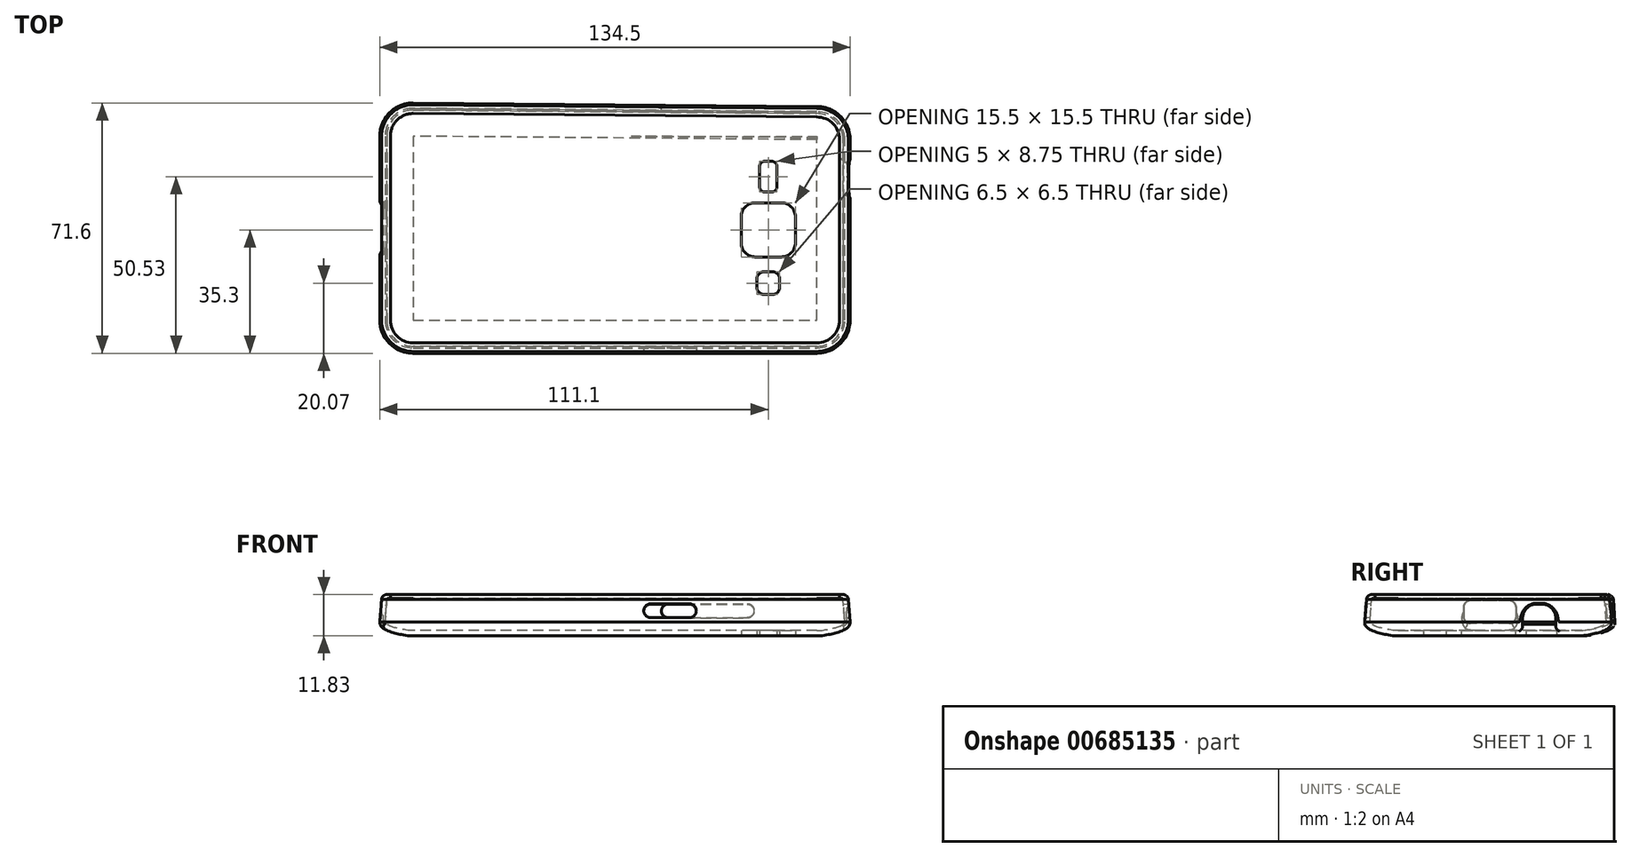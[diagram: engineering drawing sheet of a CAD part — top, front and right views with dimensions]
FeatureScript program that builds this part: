
annotation { "Feature Type Name" : "Feature", "Feature Type Description" : "" }
export const myFeature = defineFeature(function(context is Context, id is Id, definition is map)
    precondition{}
    {
        {
            var Q0;
            Q0=qCreatedBy(makeId("Front.planeOp"),FACE);
            var sketch = newSketch(context, id + "F0", { "sketchPlane" : qUnion([Q0])});
            skFitSpline(sketch, "E0", {"points": [v(23.24, 0) * mm, v(26.98, 0.47) * mm, v(29.38, 1.12) * mm, v(31.08, 2) * mm, v(31.24, 2.46) * mm], "startDerivative": vector(11.56, 0) * mm, "endDerivative": vector(0, 3.86) * mm});
            skFitSpline(sketch, "E1", {"points": [v(30.74, 9) * mm, v(30.63, 9.1) * mm, v(30.38, 9.18) * mm, v(29.74, 9.2) * mm], "startDerivative": vector(0.08, 0.24) * mm, "endDerivative": vector(-0.18, 0) * mm});
            skFitSpline(sketch, "E2.0", {"points": [v(32.24, 8.88) * mm, v(32.24, 8.97) * mm, v(32.22, 9.13) * mm, v(32.16, 9.35) * mm, v(32.08, 9.51) * mm, v(32, 9.63) * mm, v(31.92, 9.73) * mm, v(31.85, 9.8) * mm, v(31.78, 9.87) * mm, v(31.73, 9.91) * mm, v(31.67, 9.96) * mm, v(31.62, 10) * mm, v(31.56, 10.04) * mm, v(31.44, 10.12) * mm, v(31.23, 10.21) * mm, v(31.02, 10.27) * mm, v(30.85, 10.3) * mm, v(30.7, 10.31) * mm, v(30.58, 10.32) * mm, v(30.46, 10.32) * mm, v(30.34, 10.33) * mm, v(30.23, 10.33) * mm, v(30.15, 10.33) * mm, v(30.1, 10.33) * mm, v(30.06, 10.33) * mm, v(30.04, 10.33) * mm, v(30.04, 10.33) * mm, v(30.03, 10.33) * mm]});
            skFitSpline(sketch, "E3.0", {"points": [v(23.24, -1.5) * mm, v(23.79, -1.5) * mm, v(24.58, -1.45) * mm, v(25.58, -1.32) * mm, v(26.3, -1.2) * mm, v(26.96, -1.07) * mm, v(27.57, -0.94) * mm, v(28.15, -0.8) * mm, v(28.72, -0.66) * mm, v(29.28, -0.5) * mm, v(29.86, -0.3) * mm, v(30.45, -0.08) * mm, v(30.94, 0.14) * mm, v(31.32, 0.33) * mm, v(31.6, 0.5) * mm, v(31.84, 0.67) * mm, v(32.03, 0.83) * mm, v(32.19, 0.98) * mm, v(32.34, 1.16) * mm, v(32.51, 1.43) * mm, v(32.67, 1.8) * mm, v(32.74, 2.2) * mm, v(32.74, 2.39) * mm, v(32.74, 2.46) * mm]});
            skLineSegment(sketch, "E4", {"start": v(30.07, 10.33) * mm, "end": v(29.74, 10.33) * mm});
            skLineSegment(sketch, "E5", {"start": v(29.74, 10.33) * mm, "end": v(29.74, 9.2) * mm});
            skLineSegment(sketch, "E6", {"start": v(23.24, 0) * mm, "end": v(23.24, -1.5) * mm});
            skLineSegment(sketch, "E7", {"start": v(32.24, 8.88) * mm, "end": v(32.74, 2.46) * mm});
            skLineSegment(sketch, "E8", {"start": v(31.24, 2.46) * mm, "end": v(30.74, 9) * mm});
            skSolve(sketch);
        }
        {
            var Q0;
            Q0=makeQuery(id+"F0.imprint","IMPRINT",FACE,{"disambiguationData":[TD([[makeQuery(id+"F0.imprint","IMPRINT",EDGE,{"derivedFrom":sQuery(id+"F0.wireOp",EDGE,"E0")}),-1.0]])]});
            extrude(context, id + "F1", {"entities" : qUnion([Q0]), "depth" : 51.6 * mm, "offsetDistance" : 25 * mm});
        }
        {
            var Q0;
            Q0=makeQuery(id+"F1.opExtrude","CAP_FACE",FACE,{"disambiguationData":[OSD([sQuery(id+"F0.wireOp",EDGE,"E0"),sQuery(id+"F0.wireOp",EDGE,"iwZR0FTT-lc6u-Gi5J-cjGM-f3HXfoQX6Iv2"),sQuery(id+"F0.wireOp",EDGE,"E1"),sQuery(id+"F0.wireOp",EDGE,"E2.0"),sQuery(id+"F0.wireOp",EDGE,"E3.0"),sQuery(id+"F0.wireOp",EDGE,"E4"),sQuery(id+"F0.wireOp",EDGE,"E5"),sQuery(id+"F0.wireOp",EDGE,"E6"),sQuery(id+"F0.wireOp",EDGE,"pERrGrT5-6ted-8LdD-2vIX-14O5lISJ3Ztg")])],"isStart":false});
            var Q1;
            Q1=makeQuery(id+"F1.opExtrude","CAP_EDGE",EDGE,{"disambiguationData":[OSD([sQuery(id+"F0.wireOp",EDGE,"E6")])],"isStart":false});
            revolve(context, id + "F2", {"operationType" : NewBodyOperationType.ADD, "entities" : qUnion([Q0]), "axis" : qUnion([Q1]), "revolveType" : RevolveType.ONE_DIRECTION, "angle" : 90 * degree});
        }
        {
            var Q0;
            {var subQ0=sQuery(id+"F0.wireOp",EDGE,"E6");Q0=makeQuery(id+"F2.boolean.opBoolean","MERGE",FACE,{"derivedFrom":[makeQuery(id+"F1.opExtrude","SWEPT_FACE",FACE,{"disambiguationData":[OSD([subQ0])]}),makeQuery(id+"F2.opRevolve","CAP_FACE",FACE,{"disambiguationData":[OSD([sQuery(id+"F0.wireOp",EDGE,"E0"),sQuery(id+"F0.wireOp",EDGE,"iwZR0FTT-lc6u-Gi5J-cjGM-f3HXfoQX6Iv2"),sQuery(id+"F0.wireOp",EDGE,"E1"),sQuery(id+"F0.wireOp",EDGE,"E2.0"),sQuery(id+"F0.wireOp",EDGE,"E3.0"),sQuery(id+"F0.wireOp",EDGE,"E4"),sQuery(id+"F0.wireOp",EDGE,"E5"),subQ0,sQuery(id+"F0.wireOp",EDGE,"pERrGrT5-6ted-8LdD-2vIX-14O5lISJ3Ztg")])],"isStart":false})]});}
            var sketch = newSketch(context, id + "F3", { "sketchPlane" : qUnion([Q0])});
            skLineSegment(sketch, "E9", {"start": v(51.6, 0) * mm, "end": v(51.6, -1.5) * mm});
            skSolve(sketch);
        }
        {
            var Q0;
            Q0=makeQuery(id+"F3.imprint","IMPRINT",FACE,{"disambiguationData":[TD([[makeQuery(id+"F3.imprint","IMPRINT",EDGE,{"derivedFrom":sQuery(id+"F3.wireOp",EDGE,"E9")}),1.0]])]});
            extrude(context, id + "F4", {"entities" : qUnion([Q0]), "operationType" : NewBodyOperationType.ADD, "depth" : 115.5 * mm, "offsetDistance" : 25 * mm});
        }
        {
            var Q0;
            Q0=makeQuery(id+"F4.opExtrude","CAP_FACE",FACE,{"disambiguationData":[OSD([sQuery(id+"F0.wireOp",EDGE,"E0"),sQuery(id+"F0.wireOp",EDGE,"iwZR0FTT-lc6u-Gi5J-cjGM-f3HXfoQX6Iv2"),sQuery(id+"F0.wireOp",EDGE,"E1"),sQuery(id+"F0.wireOp",EDGE,"E2.0"),sQuery(id+"F0.wireOp",EDGE,"E3.0"),sQuery(id+"F0.wireOp",EDGE,"E4"),sQuery(id+"F0.wireOp",EDGE,"E5"),sQuery(id+"F0.wireOp",EDGE,"pERrGrT5-6ted-8LdD-2vIX-14O5lISJ3Ztg"),sQuery(id+"F3.wireOp",EDGE,"E9")])],"isStart":false});
            var Q1;
            Q1=makeQuery(id+"F4.opExtrude","CAP_EDGE",EDGE,{"disambiguationData":[OSD([sQuery(id+"F3.wireOp",EDGE,"E9")])],"isStart":false});
            revolve(context, id + "F5", {"operationType" : NewBodyOperationType.ADD, "entities" : qUnion([Q0]), "axis" : qUnion([Q1]), "revolveType" : RevolveType.ONE_DIRECTION, "angle" : 90 * degree});
        }
        {
            var Q0;
            {var subQ0=sQuery(id+"F3.wireOp",EDGE,"E9");Q0=makeQuery(id+"F5.boolean.opBoolean","MERGE",FACE,{"derivedFrom":[makeQuery(id+"F4.opExtrude","SWEPT_FACE",FACE,{"disambiguationData":[OSD([subQ0])]}),makeQuery(id+"F5.opRevolve","CAP_FACE",FACE,{"disambiguationData":[OSD([sQuery(id+"F0.wireOp",EDGE,"E0"),sQuery(id+"F0.wireOp",EDGE,"iwZR0FTT-lc6u-Gi5J-cjGM-f3HXfoQX6Iv2"),sQuery(id+"F0.wireOp",EDGE,"E1"),sQuery(id+"F0.wireOp",EDGE,"E2.0"),sQuery(id+"F0.wireOp",EDGE,"E3.0"),sQuery(id+"F0.wireOp",EDGE,"E4"),sQuery(id+"F0.wireOp",EDGE,"E5"),sQuery(id+"F0.wireOp",EDGE,"pERrGrT5-6ted-8LdD-2vIX-14O5lISJ3Ztg"),subQ0])],"isStart":false})]});}
            var sketch = newSketch(context, id + "F6", { "sketchPlane" : qUnion([Q0])});
            skLineSegment(sketch, "E10", {"start": v(92.26, 0) * mm, "end": v(92.26, -1.5) * mm});
            skSolve(sketch);
        }
        {
            var Q0;
            Q0=makeQuery(id+"F6.imprint","IMPRINT",FACE,{"disambiguationData":[TD([[makeQuery(id+"F6.imprint","IMPRINT",EDGE,{"derivedFrom":sQuery(id+"F6.wireOp",EDGE,"E10")}),1.0]])]});
            extrude(context, id + "F7", {"entities" : qUnion([Q0]), "operationType" : NewBodyOperationType.ADD, "depth" : 52.6 * mm, "offsetDistance" : 25 * mm});
        }
        {
            var Q0;
            Q0=makeQuery(id+"F7.opExtrude","CAP_FACE",FACE,{"disambiguationData":[OSD([sQuery(id+"F0.wireOp",EDGE,"E0"),sQuery(id+"F0.wireOp",EDGE,"iwZR0FTT-lc6u-Gi5J-cjGM-f3HXfoQX6Iv2"),sQuery(id+"F0.wireOp",EDGE,"E1"),sQuery(id+"F0.wireOp",EDGE,"E2.0"),sQuery(id+"F0.wireOp",EDGE,"E3.0"),sQuery(id+"F0.wireOp",EDGE,"E4"),sQuery(id+"F0.wireOp",EDGE,"E5"),sQuery(id+"F0.wireOp",EDGE,"pERrGrT5-6ted-8LdD-2vIX-14O5lISJ3Ztg"),sQuery(id+"F6.wireOp",EDGE,"E10")])],"isStart":false});
            var Q1;
            Q1=makeQuery(id+"F7.opExtrude","CAP_EDGE",EDGE,{"disambiguationData":[OSD([sQuery(id+"F6.wireOp",EDGE,"E10")])],"isStart":false});
            revolve(context, id + "F8", {"operationType" : NewBodyOperationType.ADD, "entities" : qUnion([Q0]), "axis" : qUnion([Q1]), "revolveType" : RevolveType.ONE_DIRECTION, "angle" : 90.5 * degree});
        }
        {
            var Q0;
            Q0=makeQuery(id+"F1.opExtrude","CAP_FACE",FACE,{"disambiguationData":[OSD([sQuery(id+"F0.wireOp",EDGE,"E0"),sQuery(id+"F0.wireOp",EDGE,"iwZR0FTT-lc6u-Gi5J-cjGM-f3HXfoQX6Iv2"),sQuery(id+"F0.wireOp",EDGE,"E1"),sQuery(id+"F0.wireOp",EDGE,"E2.0"),sQuery(id+"F0.wireOp",EDGE,"E3.0"),sQuery(id+"F0.wireOp",EDGE,"E4"),sQuery(id+"F0.wireOp",EDGE,"E5"),sQuery(id+"F0.wireOp",EDGE,"E6"),sQuery(id+"F0.wireOp",EDGE,"pERrGrT5-6ted-8LdD-2vIX-14O5lISJ3Ztg")])],"isStart":true});
            var Q1;
            Q1=makeQuery(id+"F1.opExtrude","CAP_EDGE",EDGE,{"disambiguationData":[OSD([sQuery(id+"F0.wireOp",EDGE,"E6")])],"isStart":true});
            revolve(context, id + "F9", {"operationType" : NewBodyOperationType.ADD, "entities" : qUnion([Q0]), "axis" : qUnion([Q1]), "revolveType" : RevolveType.ONE_DIRECTION, "oppositeDirection" : true, "angle" : 90 * degree});
        }
        {
            var Q0;
            {var subQ0=sQuery(id+"F0.wireOp",EDGE,"pERrGrT5-6ted-8LdD-2vIX-14O5lISJ3Ztg");var subQ1=sQuery(id+"F0.wireOp",EDGE,"E6");var subQ2=sQuery(id+"F0.wireOp",EDGE,"E5");var subQ3=sQuery(id+"F0.wireOp",EDGE,"E4");var subQ4=sQuery(id+"F0.wireOp",EDGE,"E3.0");var subQ5=sQuery(id+"F0.wireOp",EDGE,"E2.0");var subQ6=sQuery(id+"F0.wireOp",EDGE,"E1");var subQ7=sQuery(id+"F0.wireOp",EDGE,"iwZR0FTT-lc6u-Gi5J-cjGM-f3HXfoQX6Iv2");var subQ8=sQuery(id+"F0.wireOp",EDGE,"E0");Q0=makeQuery(id+"F9.boolean.opBoolean","MERGE",FACE,{"derivedFrom":[makeQuery(id+"F2.boolean.opBoolean","MERGE",FACE,{"derivedFrom":[makeQuery(id+"F1.opExtrude","SWEPT_FACE",FACE,{"disambiguationData":[OSD([subQ1])]}),makeQuery(id+"F2.opRevolve","CAP_FACE",FACE,{"disambiguationData":[OSD([subQ8,subQ7,subQ6,subQ5,subQ4,subQ3,subQ2,subQ1,subQ0])],"isStart":false})]}),makeQuery(id+"F9.opRevolve","CAP_FACE",FACE,{"disambiguationData":[OSD([subQ8,subQ7,subQ6,subQ5,subQ4,subQ3,subQ2,subQ1,subQ0])],"isStart":false})]});}
            var sketch = newSketch(context, id + "F10", { "sketchPlane" : qUnion([Q0])});
            skLineSegment(sketch, "E11", {"start": v(0, 0) * mm, "end": v(0, -1.5) * mm});
            skSolve(sketch);
        }
        {
            var Q1;
            Q1=makeQuery(id+"F10.imprint","IMPRINT",FACE,{"disambiguationData":[TD([[makeQuery(id+"F10.imprint","IMPRINT",EDGE,{"derivedFrom":sQuery(id+"F10.wireOp",EDGE,"E11")}),-1.0]])]});
            var Q2;
            Q2=makeQuery(id+"F8.opRevolve","CAP_FACE",FACE,{"disambiguationData":[OSD([sQuery(id+"F0.wireOp",EDGE,"E0"),sQuery(id+"F0.wireOp",EDGE,"iwZR0FTT-lc6u-Gi5J-cjGM-f3HXfoQX6Iv2"),sQuery(id+"F0.wireOp",EDGE,"E1"),sQuery(id+"F0.wireOp",EDGE,"E2.0"),sQuery(id+"F0.wireOp",EDGE,"E3.0"),sQuery(id+"F0.wireOp",EDGE,"E4"),sQuery(id+"F0.wireOp",EDGE,"E5"),sQuery(id+"F0.wireOp",EDGE,"pERrGrT5-6ted-8LdD-2vIX-14O5lISJ3Ztg"),sQuery(id+"F6.wireOp",EDGE,"E10")])],"isStart":false});
            loft(context, id + "F11", {"operationType" : NewBodyOperationType.ADD, "sheetProfilesArray" : [{ "sheetProfileEntities" : qUnion([Q1]) }, { "sheetProfileEntities" : qUnion([Q2]) }]});
        }
        {
            var Q0;
            Q0=makeQuery(id+"F7.opExtrude","SWEPT_FACE",FACE,{"disambiguationData":[OSD([sQuery(id+"F6.wireOp",EDGE,"E10")])]});
            extrude(context, id + "F12", {"entities" : qUnion([Q0]), "operationType" : NewBodyOperationType.ADD, "depth" : 115.5 * mm, "offsetDistance" : 25 * mm});
        }
        {
            var Q0;
            Q0=makeQuery(id+"F12.opExtrude","SWEPT_FACE",FACE,{"disambiguationData":[OSD([sQuery(id+"F0.wireOp",EDGE,"E3.0"),sQuery(id+"F0.wireOp",EDGE,"E6"),sQuery(id+"F3.wireOp",EDGE,"E9"),sQuery(id+"F6.wireOp",EDGE,"E10")])]});
            var sketch = newSketch(context, id + "F13", { "sketchPlane" : qUnion([Q0])});
            skPoint(sketch, "E12", {"position": v(9.34, 25.8) * mm});
            skPoint(sketch, "E12.positionSnap0", {"position": v(23.24, 25.8) * mm});
            skLineSegment(sketch, "E13.bottom", {"start": v(13.09, 33.55) * mm, "end": v(5.59, 33.55) * mm});
            skLineSegment(sketch, "E13.top", {"start": v(13.09, 18.05) * mm, "end": v(5.59, 18.05) * mm});
            skLineSegment(sketch, "E13.left", {"start": v(17.09, 29.55) * mm, "end": v(17.09, 22.05) * mm});
            skLineSegment(sketch, "E13.right", {"start": v(1.59, 29.55) * mm, "end": v(1.59, 22.05) * mm});
            skPoint(sketch, "E14.visualSharp", {"position": v(17.09, 33.55) * mm});
            skArc(sketch, "E14.filletArc", {"start": v(17.09, 29.55) * mm, "mid": v(15.92, 32.38) * mm, "end": v(13.09, 33.55) * mm});
            skPoint(sketch, "E15.visualSharp", {"position": v(17.09, 18.05) * mm});
            skArc(sketch, "E15.filletArc", {"start": v(13.09, 18.05) * mm, "mid": v(15.92, 19.22) * mm, "end": v(17.09, 22.05) * mm});
            skPoint(sketch, "E16.visualSharp", {"position": v(1.59, 18.05) * mm});
            skArc(sketch, "E16.filletArc", {"start": v(1.59, 22.05) * mm, "mid": v(2.76, 19.22) * mm, "end": v(5.59, 18.05) * mm});
            skPoint(sketch, "E17.visualSharp", {"position": v(1.59, 33.55) * mm});
            skArc(sketch, "E17.filletArc", {"start": v(5.59, 33.55) * mm, "mid": v(2.76, 32.38) * mm, "end": v(1.59, 29.55) * mm});
            skPoint(sketch, "E18", {"position": v(9.34, 41.03) * mm});
            skLineSegment(sketch, "E19.bottom", {"start": v(10.59, 37.78) * mm, "end": v(8.09, 37.78) * mm});
            skLineSegment(sketch, "E19.top", {"start": v(10.59, 44.28) * mm, "end": v(8.09, 44.28) * mm});
            skLineSegment(sketch, "E19.left", {"start": v(12.59, 39.78) * mm, "end": v(12.59, 42.28) * mm});
            skLineSegment(sketch, "E19.right", {"start": v(6.09, 39.78) * mm, "end": v(6.09, 42.28) * mm});
            skPoint(sketch, "E20.visualSharp", {"position": v(12.59, 44.28) * mm});
            skArc(sketch, "E20.filletArc", {"start": v(12.59, 42.28) * mm, "mid": v(12, 43.7) * mm, "end": v(10.59, 44.28) * mm});
            skPoint(sketch, "E21.visualSharp", {"position": v(12.59, 37.78) * mm});
            skArc(sketch, "E21.filletArc", {"start": v(10.59, 37.78) * mm, "mid": v(12, 38.37) * mm, "end": v(12.59, 39.78) * mm});
            skPoint(sketch, "E22.visualSharp", {"position": v(6.09, 37.78) * mm});
            skArc(sketch, "E22.filletArc", {"start": v(6.09, 39.78) * mm, "mid": v(6.68, 38.37) * mm, "end": v(8.09, 37.78) * mm});
            skPoint(sketch, "E23.visualSharp", {"position": v(6.09, 44.28) * mm});
            skArc(sketch, "E23.filletArc", {"start": v(8.09, 44.28) * mm, "mid": v(6.68, 43.7) * mm, "end": v(6.09, 42.28) * mm});
            skPoint(sketch, "E24", {"position": v(9.34, 10.57) * mm});
            skLineSegment(sketch, "E25.bottom", {"start": v(10.34, 6.2) * mm, "end": v(8.34, 6.2) * mm});
            skLineSegment(sketch, "E25.top", {"start": v(10.34, 14.95) * mm, "end": v(8.34, 14.95) * mm});
            skLineSegment(sketch, "E25.left", {"start": v(11.84, 7.7) * mm, "end": v(11.84, 13.45) * mm});
            skLineSegment(sketch, "E25.right", {"start": v(6.84, 7.7) * mm, "end": v(6.84, 13.45) * mm});
            skPoint(sketch, "E26.visualSharp", {"position": v(11.84, 14.95) * mm});
            skArc(sketch, "E26.filletArc", {"start": v(11.84, 13.45) * mm, "mid": v(11.4, 14.5) * mm, "end": v(10.34, 14.95) * mm});
            skPoint(sketch, "E27.visualSharp", {"position": v(6.84, 14.95) * mm});
            skArc(sketch, "E27.filletArc", {"start": v(8.34, 14.95) * mm, "mid": v(7.28, 14.5) * mm, "end": v(6.84, 13.45) * mm});
            skPoint(sketch, "E28.visualSharp", {"position": v(6.84, 6.2) * mm});
            skArc(sketch, "E28.filletArc", {"start": v(6.84, 7.7) * mm, "mid": v(7.28, 6.63) * mm, "end": v(8.34, 6.2) * mm});
            skPoint(sketch, "E29.visualSharp", {"position": v(11.84, 6.2) * mm});
            skArc(sketch, "E29.filletArc", {"start": v(10.34, 6.2) * mm, "mid": v(11.4, 6.63) * mm, "end": v(11.84, 7.7) * mm});
            skSolve(sketch);
        }
        {
            var Q0;
            Q0=makeQuery(id+"F13.imprint","IMPRINT",FACE,{"disambiguationData":[TD([[makeQuery(id+"F13.imprint","IMPRINT",EDGE,{"derivedFrom":sQuery(id+"F13.wireOp",EDGE,"E19.bottom")}),-1.0]])]});
            var Q1;
            Q1=makeQuery(id+"F13.imprint","IMPRINT",FACE,{"disambiguationData":[TD([[makeQuery(id+"F13.imprint","IMPRINT",EDGE,{"derivedFrom":sQuery(id+"F13.wireOp",EDGE,"E13.bottom")}),1.0]])]});
            var Q2;
            Q2=makeQuery(id+"F13.imprint","IMPRINT",FACE,{"disambiguationData":[TD([[makeQuery(id+"F13.imprint","IMPRINT",EDGE,{"derivedFrom":sQuery(id+"F13.wireOp",EDGE,"E25.bottom")}),-1.0]])]});
            extrude(context, id + "F14", {"entities" : qUnion([Q0, Q1, Q2]), "operationType" : NewBodyOperationType.REMOVE, "oppositeDirection" : true, "depth" : 4 * mm, "offsetDistance" : 25 * mm});
        }
        {
            var Q0;
            Q0=makeQuery(id+"F11.opLoft","SWEPT_FACE",FACE,{"disambiguationData":[OSD([sQuery(id+"F0.wireOp",EDGE,"E2.0"),sQuery(id+"F0.wireOp",EDGE,"E3.0"),sQuery(id+"F0.wireOp",EDGE,"pERrGrT5-6ted-8LdD-2vIX-14O5lISJ3Ztg")])]});
            var sketch = newSketch(context, id + "F15", { "sketchPlane" : qUnion([Q0])});
            skPoint(sketch, "E30", {"position": v(8.06, 4.94) * mm});
            skPoint(sketch, "E30.positionSnap0", {"position": v(-23.16, 4.94) * mm});
            skLineSegment(sketch, "E31.bottom", {"start": v(19.31, 6.94) * mm, "end": v(-3.19, 6.94) * mm});
            skLineSegment(sketch, "E31.top", {"start": v(19.31, 2.94) * mm, "end": v(-3.19, 2.94) * mm});
            skLineSegment(sketch, "E31.left", {"start": v(21.31, 4.94) * mm, "end": v(21.31, 4.94) * mm});
            skLineSegment(sketch, "E31.right", {"start": v(-5.19, 4.94) * mm, "end": v(-5.19, 4.94) * mm});
            skPoint(sketch, "E32.visualSharp", {"position": v(-5.19, 6.94) * mm});
            skArc(sketch, "E32.filletArc", {"start": v(-3.19, 6.94) * mm, "mid": v(-4.6, 6.35) * mm, "end": v(-5.19, 4.94) * mm});
            skPoint(sketch, "E33.visualSharp", {"position": v(-5.19, 2.94) * mm});
            skArc(sketch, "E33.filletArc", {"start": v(-5.19, 4.94) * mm, "mid": v(-4.6, 3.52) * mm, "end": v(-3.19, 2.94) * mm});
            skPoint(sketch, "E34.visualSharp", {"position": v(21.31, 6.94) * mm});
            skArc(sketch, "E34.filletArc", {"start": v(21.31, 4.94) * mm, "mid": v(20.72, 6.35) * mm, "end": v(19.31, 6.94) * mm});
            skPoint(sketch, "E35.visualSharp", {"position": v(21.31, 2.94) * mm});
            skArc(sketch, "E35.filletArc", {"start": v(19.31, 2.94) * mm, "mid": v(20.72, 3.52) * mm, "end": v(21.31, 4.94) * mm});
            skSolve(sketch);
        }
        {
            var Q0;
            Q0=makeQuery(id+"F15.imprint","IMPRINT",FACE,{"disambiguationData":[TD([[makeQuery(id+"F15.imprint","IMPRINT",EDGE,{"derivedFrom":sQuery(id+"F15.wireOp",EDGE,"E31.bottom")}),1.0]])]});
            extrude(context, id + "F16", {"entities" : qUnion([Q0]), "operationType" : NewBodyOperationType.REMOVE, "oppositeDirection" : true, "depth" : 3 * mm, "offsetDistance" : 25 * mm});
        }
        {
            var Q0;
            Q0=makeQuery(id+"F7.opExtrude","SWEPT_FACE",FACE,{"disambiguationData":[OSD([sQuery(id+"F0.wireOp",EDGE,"E7")])]});
            var sketch = newSketch(context, id + "F17", { "sketchPlane" : qUnion([Q0])});
            skLineSegment(sketch, "E36.bottom", {"start": v(30.8, 0.75) * mm, "end": v(19.8, 0.75) * mm});
            skLineSegment(sketch, "E36.top", {"start": v(30.8, -5.75) * mm, "end": v(19.8, -5.75) * mm});
            skLineSegment(sketch, "E36.left", {"start": v(32.8, -1.25) * mm, "end": v(32.8, -3.75) * mm});
            skLineSegment(sketch, "E36.right", {"start": v(17.8, -1.25) * mm, "end": v(17.8, -3.75) * mm});
            skPoint(sketch, "E36.middle", {"position": v(25.3, -2.5) * mm});
            skPoint(sketch, "E36.middle.positionSnap0", {"position": v(25.3, 1) * mm});
            skPoint(sketch, "E36.centerSnap0", {"position": v(25.3, 1) * mm});
            skPoint(sketch, "E37.visualSharp", {"position": v(17.8, 0.75) * mm});
            skArc(sketch, "E37.filletArc", {"start": v(19.8, 0.75) * mm, "mid": v(18.39, 0.16) * mm, "end": v(17.8, -1.25) * mm});
            skPoint(sketch, "E38.visualSharp", {"position": v(32.8, 0.75) * mm});
            skArc(sketch, "E38.filletArc", {"start": v(32.8, -1.25) * mm, "mid": v(32.21, 0.16) * mm, "end": v(30.8, 0.75) * mm});
            skPoint(sketch, "E39.visualSharp", {"position": v(32.8, -5.75) * mm});
            skArc(sketch, "E39.filletArc", {"start": v(30.8, -5.75) * mm, "mid": v(32.21, -5.16) * mm, "end": v(32.8, -3.75) * mm});
            skPoint(sketch, "E40.visualSharp", {"position": v(17.8, -5.75) * mm});
            skArc(sketch, "E40.filletArc", {"start": v(17.8, -3.75) * mm, "mid": v(18.39, -5.16) * mm, "end": v(19.8, -5.75) * mm});
            skSolve(sketch);
        }
        {
            var Q0;
            Q0 = qSketchRegion(id + "F17", true);
            extrude(context, id + "F18", {"entities" : qUnion([Q0]), "operationType" : NewBodyOperationType.REMOVE, "oppositeDirection" : true, "depth" : 4 * mm, "offsetDistance" : 25 * mm});
        }
        {
            var Q0;
            Q0=makeQuery(id+"F4.opExtrude","SWEPT_FACE",FACE,{"disambiguationData":[OSD([sQuery(id+"F0.wireOp",EDGE,"E7")])]});
            var sketch = newSketch(context, id + "F19", { "sketchPlane" : qUnion([Q0])});
            skLineSegment(sketch, "E41.bottom", {"start": v(-13.26, 2.93) * mm, "end": v(-24.26, 2.93) * mm});
            skLineSegment(sketch, "E41.top", {"start": v(-13.26, -1.07) * mm, "end": v(-24.26, -1.07) * mm});
            skLineSegment(sketch, "E41.left", {"start": v(-11.26, 0.93) * mm, "end": v(-11.26, 0.93) * mm});
            skLineSegment(sketch, "E41.right", {"start": v(-26.26, 0.93) * mm, "end": v(-26.26, 0.93) * mm});
            skPoint(sketch, "E41.middle", {"position": v(-18.76, 0.93) * mm});
            skPoint(sketch, "E41.middle.positionSnap0", {"position": v(23.24, 0.93) * mm});
            skPoint(sketch, "E41.centerSnap0", {"position": v(23.24, 0.93) * mm});
            skPoint(sketch, "E42.visualSharp", {"position": v(-26.26, 2.93) * mm});
            skArc(sketch, "E42.filletArc", {"start": v(-24.26, 2.93) * mm, "mid": v(-25.67, 2.35) * mm, "end": v(-26.26, 0.93) * mm});
            skPoint(sketch, "E43.visualSharp", {"position": v(-26.26, -1.07) * mm});
            skArc(sketch, "E43.filletArc", {"start": v(-26.26, 0.93) * mm, "mid": v(-25.67, -0.48) * mm, "end": v(-24.26, -1.07) * mm});
            skPoint(sketch, "E44.visualSharp", {"position": v(-11.26, -1.07) * mm});
            skArc(sketch, "E44.filletArc", {"start": v(-13.26, -1.07) * mm, "mid": v(-11.85, -0.48) * mm, "end": v(-11.26, 0.93) * mm});
            skPoint(sketch, "E45.visualSharp", {"position": v(-11.26, 2.93) * mm});
            skArc(sketch, "E45.filletArc", {"start": v(-11.26, 0.93) * mm, "mid": v(-11.85, 2.35) * mm, "end": v(-13.26, 2.93) * mm});
            skSolve(sketch);
        }
        {
            var Q0;
            Q0 = qSketchRegion(id + "F19", true);
            extrude(context, id + "F20", {"entities" : qUnion([Q0]), "operationType" : NewBodyOperationType.REMOVE, "oppositeDirection" : true, "depth" : 5 * mm, "offsetDistance" : 25 * mm});
        }
        {
            var Q0;
            Q0=makeQuery(id+"F1.opExtrude","SWEPT_FACE",FACE,{"disambiguationData":[OSD([sQuery(id+"F0.wireOp",EDGE,"E7")])]});
            var sketch = newSketch(context, id + "F21", { "sketchPlane" : qUnion([Q0])});
            skLineSegment(sketch, "E46.bottom", {"start": v(-15.94, -4.34) * mm, "end": v(-6.44, -4.34) * mm});
            skLineSegment(sketch, "E46.top", {"start": v(-11.94, 5.16) * mm, "end": v(-10.44, 5.16) * mm});
            skLineSegment(sketch, "E46.left", {"start": v(-15.94, -4.34) * mm, "end": v(-15.94, 1.16) * mm});
            skLineSegment(sketch, "E46.right", {"start": v(-6.44, -4.34) * mm, "end": v(-6.44, 1.16) * mm});
            skPoint(sketch, "E46.middle", {"position": v(-11.19, 0.41) * mm});
            skPoint(sketch, "E47.visualSharp", {"position": v(-6.44, 5.16) * mm});
            skArc(sketch, "E47.filletArc", {"start": v(-6.44, 1.16) * mm, "mid": v(-7.6, 4) * mm, "end": v(-10.44, 5.16) * mm});
            skPoint(sketch, "E48.visualSharp", {"position": v(-15.94, 5.16) * mm});
            skArc(sketch, "E48.filletArc", {"start": v(-11.94, 5.16) * mm, "mid": v(-14.76, 4) * mm, "end": v(-15.94, 1.16) * mm});
            skSolve(sketch);
        }
        {
            var Q0;
            Q0=makeQuery(id+"F21.imprint","IMPRINT",FACE,{"disambiguationData":[TD([[makeQuery(id+"F21.imprint","IMPRINT",EDGE,{"derivedFrom":sQuery(id+"F21.wireOp",EDGE,"E46.top")}),-1.0]])]});
            var Q1;
            {var subQ0=sQuery(id+"F21.wireOp",EDGE,"E46.bottom");Q1=makeQuery(id+"F21.imprint","IMPRINT",FACE,{"disambiguationData":[TD([[makeQuery(id+"F21.imprint","IMPRINT",EDGE,{"derivedFrom":subQ0}),1.0]])]});}
            extrude(context, id + "F22", {"entities" : qUnion([Q0, Q1]), "operationType" : NewBodyOperationType.REMOVE, "oppositeDirection" : true, "depth" : 2 * mm, "offsetDistance" : 25 * mm});
        }
        {
            var Q0;
            Q0=makeQuery(id+"F14.boolean.opBoolean","COPY",EDGE,{"derivedFrom":makeQuery(id+"F14.opExtrude","CAP_EDGE",EDGE,{"disambiguationData":[OSD([sQuery(id+"F13.wireOp",EDGE,"E25.right")])],"isStart":true})});
            var Q1;
            Q1=makeQuery(id+"F14.boolean.opBoolean","COPY",EDGE,{"derivedFrom":makeQuery(id+"F14.opExtrude","CAP_EDGE",EDGE,{"disambiguationData":[OSD([sQuery(id+"F13.wireOp",EDGE,"E13.right")])],"isStart":true})});
            var Q2;
            Q2=makeQuery(id+"F22.boolean.opBoolean","INTERSECT",EDGE,{"derivedFrom":[makeQuery(id+"F1.opExtrude","SWEPT_FACE",FACE,{"disambiguationData":[OSD([sQuery(id+"F0.wireOp",EDGE,"E3.0")])]}),makeQuery(id+"F22.opExtrude","CAP_FACE",FACE,{"disambiguationData":[OSD([sQuery(id+"F21.wireOp",EDGE,"E46.bottom"),sQuery(id+"F21.wireOp",EDGE,"E46.top"),sQuery(id+"F21.wireOp",EDGE,"E46.left"),sQuery(id+"F21.wireOp",EDGE,"E46.right"),sQuery(id+"F21.wireOp",EDGE,"E47.filletArc"),sQuery(id+"F21.wireOp",EDGE,"E48.filletArc")])],"isStart":false})]});
            var Q3;
            Q3=makeQuery(id+"F22.boolean.opBoolean","INTERSECT",EDGE,{"derivedFrom":[makeQuery(id+"F1.opExtrude","SWEPT_FACE",FACE,{"disambiguationData":[OSD([sQuery(id+"F0.wireOp",EDGE,"E3.0")])]}),makeQuery(id+"F22.opExtrude","SWEPT_FACE",FACE,{"disambiguationData":[OSD([sQuery(id+"F21.wireOp",EDGE,"E46.left")])]})]});
            var Q4;
            Q4=makeQuery(id+"F22.boolean.opBoolean","COPY",EDGE,{"derivedFrom":makeQuery(id+"F22.opExtrude","CAP_EDGE",EDGE,{"disambiguationData":[OSD([sQuery(id+"F21.wireOp",EDGE,"E47.filletArc")])],"isStart":true})});
            var Q5;
            Q5=makeQuery(id+"F22.boolean.opBoolean","INTERSECT",EDGE,{"derivedFrom":[makeQuery(id+"F1.opExtrude","SWEPT_FACE",FACE,{"disambiguationData":[OSD([sQuery(id+"F0.wireOp",EDGE,"E3.0")])]}),makeQuery(id+"F22.opExtrude","SWEPT_FACE",FACE,{"disambiguationData":[OSD([sQuery(id+"F21.wireOp",EDGE,"E46.right")])]})]});
            var Q6;
            Q6=makeQuery(id+"F14.boolean.opBoolean","COPY",EDGE,{"derivedFrom":makeQuery(id+"F14.opExtrude","CAP_EDGE",EDGE,{"disambiguationData":[OSD([sQuery(id+"F13.wireOp",EDGE,"E19.right")])],"isStart":true})});
            var Q7;
            Q7=makeQuery(id+"F16.boolean.opBoolean","COPY",EDGE,{"derivedFrom":makeQuery(id+"F16.opExtrude","CAP_EDGE",EDGE,{"disambiguationData":[OSD([sQuery(id+"F15.wireOp",EDGE,"E31.bottom")])],"isStart":true})});
            var Q8;
            Q8=makeQuery(id+"F20.boolean.opBoolean","COPY",EDGE,{"derivedFrom":makeQuery(id+"F20.opExtrude","CAP_EDGE",EDGE,{"disambiguationData":[OSD([sQuery(id+"F19.wireOp",EDGE,"E41.bottom")])],"isStart":true})});
            var Q9;
            Q9=makeQuery(id+"F18.boolean.opBoolean","COPY",EDGE,{"derivedFrom":makeQuery(id+"F18.opExtrude","CAP_EDGE",EDGE,{"disambiguationData":[OSD([sQuery(id+"F17.wireOp",EDGE,"E36.right")])],"isStart":true})});
            var Q10;
            Q10=makeQuery(id+"F18.boolean.opBoolean","INTERSECT",EDGE,{"derivedFrom":[makeQuery(id+"F7.opExtrude","SWEPT_FACE",FACE,{"disambiguationData":[OSD([sQuery(id+"F0.wireOp",EDGE,"E3.0")])]}),makeQuery(id+"F18.opExtrude","SWEPT_FACE",FACE,{"disambiguationData":[OSD([sQuery(id+"F17.wireOp",EDGE,"E36.top")])]})]});
            fillet(context, id + "F23", {"entities" : qUnion([Q0, Q1, Q2, Q3, Q4, Q5, Q6, Q7, Q8, Q9, Q10]), "radius" : 1 * mm, "tangentPropagation" : true, "allowEdgeOverflow" : false});
        }
    });
